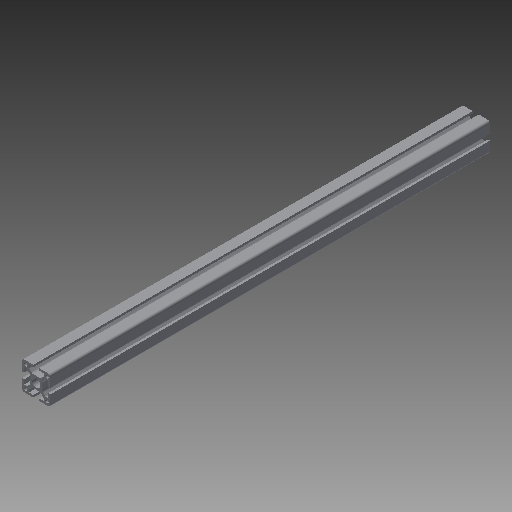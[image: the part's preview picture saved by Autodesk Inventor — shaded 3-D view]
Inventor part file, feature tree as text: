
AUTODESK INVENTOR PART (.ipt)
format: ipt  version: 2018 (Build 220112000, 112)  size: 224,256 bytes
history: native  units: mm
features: other x42, sketch x5, hole x4, extrude x1
ambient origin geometry x8: Origin, YZ Plane, XZ Plane, XY Plane, X Axis, Y Axis, Z Axis, Center Point
bodies: Solid1 (feature_tree)
feature tree (52):
  extrude  "Extrusion1"  [1 undecoded]
  hole  "Drilling 1"  [1 undecoded]
  hole  "Drilling 2"  [1 undecoded]
  hole  "Drilling 3"  [1 undecoded]
  hole  "Drilling 4"  [1 undecoded]
  other  "side_4d_XY"
  other  "side_4d_YZ"
  other  "side_4d_ZX"
  other  "side_4d_X"
  other  "side_4d_Y"
  other  "side_4d_Z"
  other  "side_4d_Center"
  other  "side_1a_XY"
  other  "side_1a_YZ"
  other  "side_1a_ZX"
  other  "side_1a_X"
  other  "side_1a_Y"
  other  "side_1a_Z"
  other  "side_1a_Center"
  other  "side_2b_XY"
  other  "side_2b_YZ"
  other  "side_2b_ZX"
  other  "side_2b_X"
  other  "side_2b_Y"
  other  "side_2b_Z"
  other  "side_2b_Center"
  other  "side_3c_XY"
  other  "side_3c_YZ"
  other  "side_3c_ZX"
  other  "side_3c_X"
  other  "side_3c_Y"
  other  "side_3c_Z"
  other  "side_3c_Center"
  other  "end_XY"
  other  "end_YZ"
  other  "end_ZX"
  other  "end_X"
  other  "end_Y"
  other  "end_Z"
  other  "end_Center"
  other  "start_XY"
  other  "start_YZ"
  other  "start_ZX"
  other  "start_X"
  other  "start_Y"
  other  "start_Z"
  other  "start_Center"
  sketch  "Skizze_1"  dims[d0=620.0mm d1=0.0mm]
  sketch  "Sketch2"  dims[d2=5.0mm d3=6.0mm d4=4.0mm d5=2.0mm d6=90.0deg d7=6000.0mm d8=0.0mm]
  sketch  "Sketch3"  dims[d9=5.0mm d10=6.0mm d11=4.0mm d12=2.0mm d13=90.0deg d14=6000.0mm d15=0.0mm]
  sketch  "Sketch4"  dims[d16=5.0mm d17=6.0mm d18=4.0mm d19=2.0mm d20=90.0deg d21=6000.0mm d22=0.0mm]
  sketch  "Sketch5"  dims[d23=5.0mm d24=6.0mm d25=4.0mm d26=2.0mm d27=90.0deg d28=6000.0mm d29=0.0mm]
note: 5 required parameter values undecoded (feature->parameter linkage not recoverable at this tier; creation-order binding heuristic only, values carry confidence <= 0.55)
